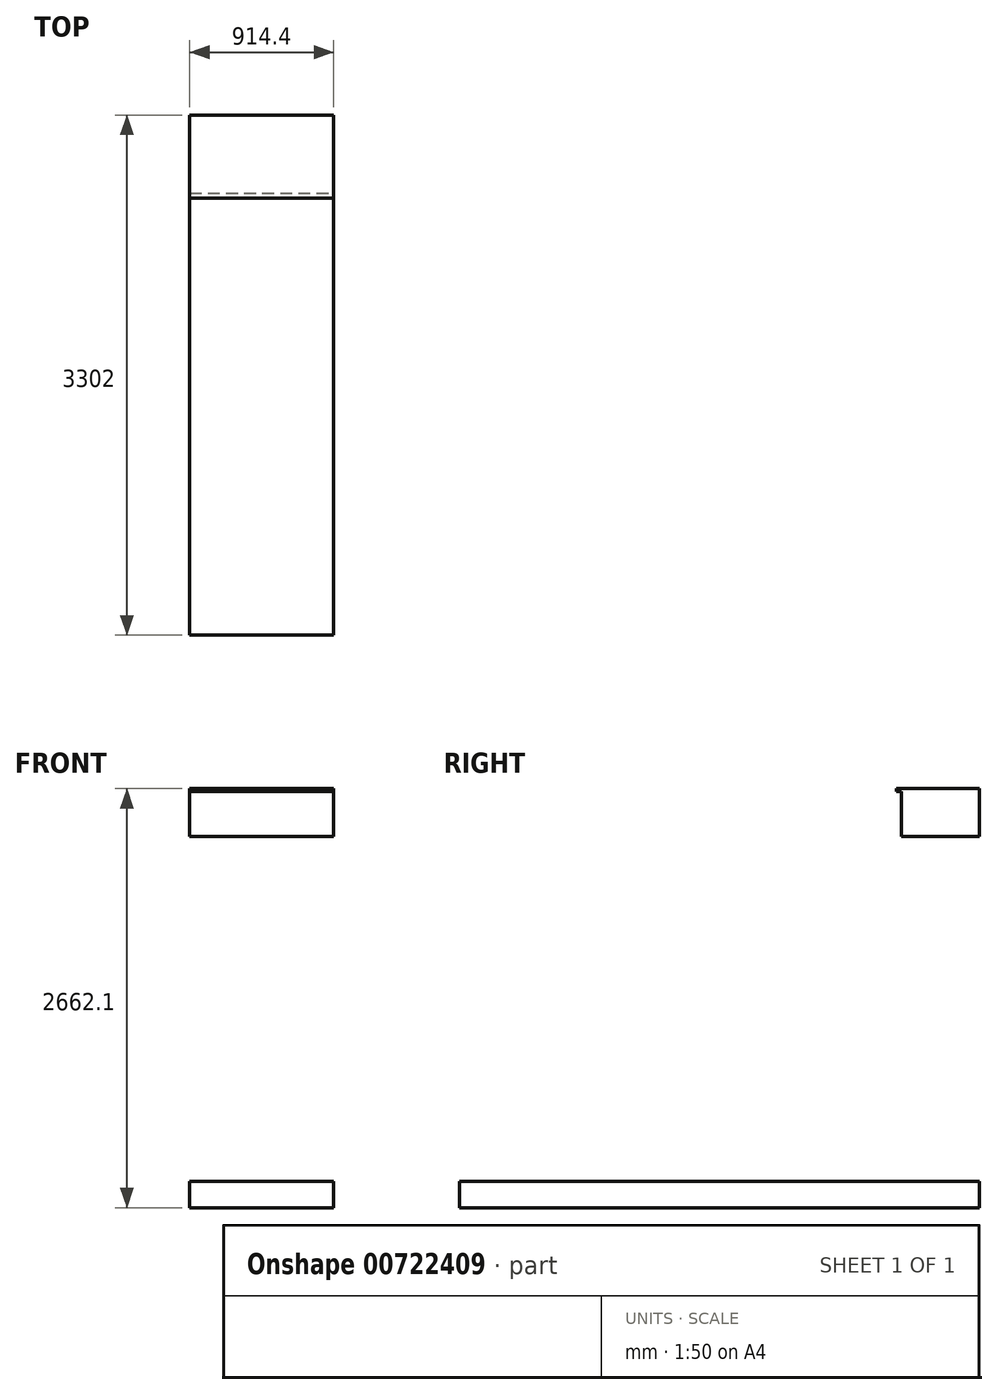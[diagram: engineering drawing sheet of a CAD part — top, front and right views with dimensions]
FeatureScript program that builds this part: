
annotation { "Feature Type Name" : "Feature", "Feature Type Description" : "" }
export const myFeature = defineFeature(function(context is Context, id is Id, definition is map)
    precondition{}
    {
        {
            var Q0;
            Q0=qCreatedBy(makeId("Right.planeOp"),FACE);
            var sketch = newSketch(context, id + "F0", { "sketchPlane" : qUnion([Q0])});
            skLineSegment(sketch, "E0.bottom", {"start": v(0, 2190.75) * mm, "end": v(-495.3, 2190.75) * mm});
            skLineSegment(sketch, "E0.top", {"start": v(0, 2495.55) * mm, "end": v(-495.3, 2495.55) * mm});
            skLineSegment(sketch, "E0.left", {"start": v(0, 2190.75) * mm, "end": v(0, 2495.55) * mm});
            skLineSegment(sketch, "E0.right", {"start": v(-495.3, 2190.75) * mm, "end": v(-495.3, 2495.55) * mm});
            skSolve(sketch);
        }
        {
            var Q0;
            Q0=makeQuery(id+"F0.imprint","IMPRINT",FACE,{"disambiguationData":[TD([[makeQuery(id+"F0.imprint","IMPRINT",EDGE,{"derivedFrom":sQuery(id+"F0.wireOp",EDGE,"E0.bottom")}),-1.0]])]});
            extrude(context, id + "F1", {"entities" : qUnion([Q0]), "oppositeDirection" : true, "depth" : 914.4 * mm, "offsetDistance" : 25.4 * mm});
        }
        {
            var Q0;
            Q0=makeQuery(id+"F1.opExtrude","CAP_FACE",FACE,{"disambiguationData":[OSD([sQuery(id+"F0.wireOp",EDGE,"E0.bottom"),sQuery(id+"F0.wireOp",EDGE,"E0.top"),sQuery(id+"F0.wireOp",EDGE,"E0.left"),sQuery(id+"F0.wireOp",EDGE,"E0.right")])],"isStart":true});
            var sketch = newSketch(context, id + "F2", { "sketchPlane" : qUnion([Q0])});
            skLineSegment(sketch, "E1.bottom", {"start": v(-495.3, 2495.55) * mm, "end": v(-527.05, 2495.55) * mm});
            skLineSegment(sketch, "E1.top", {"start": v(-495.3, 2476.5) * mm, "end": v(-527.05, 2476.5) * mm});
            skLineSegment(sketch, "E1.left", {"start": v(-495.3, 2495.55) * mm, "end": v(-495.3, 2476.5) * mm});
            skLineSegment(sketch, "E1.right", {"start": v(-527.05, 2495.55) * mm, "end": v(-527.05, 2476.5) * mm});
            skSolve(sketch);
        }
        {
            var Q0;
            Q0 = qSketchRegion(id + "F2", true);
            var Q1;
            Q1=makeQuery(id+"F1.opExtrude","CAP_VERTEX",VERTEX,{"disambiguationData":[OSD([sQuery(id+"F0.wireOp",EDGE,"E0.top"),sQuery(id+"F0.wireOp",EDGE,"E0.right")])],"isStart":false});
            extrude(context, id + "F3", {"entities" : qUnion([Q0]), "operationType" : NewBodyOperationType.ADD, "endBound" : BoundingType.UP_TO_VERTEX, "oppositeDirection" : true, "depth" : 25.4 * mm, "endBoundEntityVertex" : qUnion([Q1]), "offsetDistance" : 25.4 * mm});
        }
        {
            var Q0;
            Q0=qCreatedBy(makeId("Right.planeOp"),FACE);
            var sketch = newSketch(context, id + "F4", { "sketchPlane" : qUnion([Q0])});
            skLineSegment(sketch, "E2.bottom", {"start": v(0, 0) * mm, "end": v(-3302, 0) * mm});
            skLineSegment(sketch, "E2.top", {"start": v(0, -166.55) * mm, "end": v(-3302, -166.55) * mm});
            skLineSegment(sketch, "E2.left", {"start": v(0, 0) * mm, "end": v(0, -166.55) * mm});
            skLineSegment(sketch, "E2.right", {"start": v(-3302, 0) * mm, "end": v(-3302, -166.55) * mm});
            skSolve(sketch);
        }
        {
            var Q0;
            Q0=makeQuery(id+"F4.imprint","IMPRINT",FACE,{"disambiguationData":[TD([[makeQuery(id+"F4.imprint","IMPRINT",EDGE,{"derivedFrom":sQuery(id+"F4.wireOp",EDGE,"E2.bottom")}),1.0]])]});
            extrude(context, id + "F5", {"entities" : qUnion([Q0]), "oppositeDirection" : true, "depth" : 914.4 * mm, "offsetDistance" : 25.4 * mm});
        }
    });
